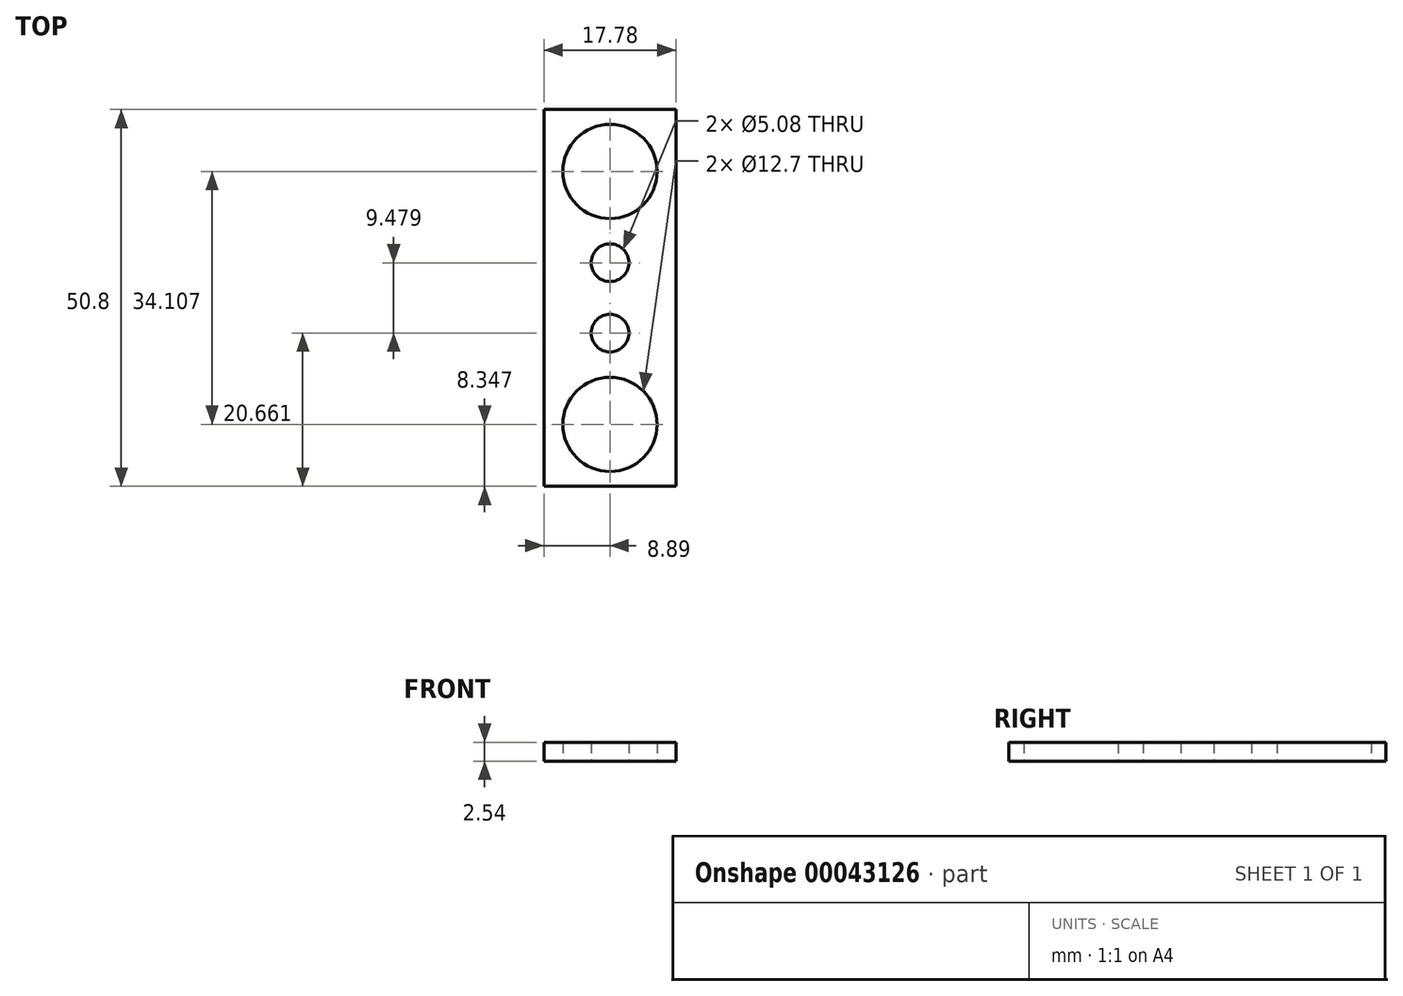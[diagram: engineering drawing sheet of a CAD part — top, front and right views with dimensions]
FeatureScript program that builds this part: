
annotation { "Feature Type Name" : "Feature", "Feature Type Description" : "" }
export const myFeature = defineFeature(function(context is Context, id is Id, definition is map)
    precondition{}
    {
        {
            var Q0;
            Q0=qCreatedBy(makeId("Top.planeOp"),FACE);
            var sketch = newSketch(context, id + "F0", { "sketchPlane" : qUnion([Q0])});
            skLineSegment(sketch, "E0.bottom", {"start": v(8.89, 25.4) * mm, "end": v(-8.9, 25.4) * mm});
            skLineSegment(sketch, "E0.top", {"start": v(8.9, -25.4) * mm, "end": v(-8.89, -25.4) * mm});
            skLineSegment(sketch, "E0.left", {"start": v(8.89, 25.4) * mm, "end": v(8.9, -25.4) * mm});
            skLineSegment(sketch, "E0.right", {"start": v(-8.9, 25.4) * mm, "end": v(-8.89, -25.4) * mm});
            skPoint(sketch, "E0.middle", {"position": v(0, 0) * mm});
            skCircle(sketch, "E1", {"center": v(0, 17.05) * mm, "radius": 6.35 * mm});
            skPoint(sketch, "E1.centerSnap0", {"position": v(0, 25.4) * mm});
            skCircle(sketch, "E2.MirrorC", {"center": v(0, -17.05) * mm, "radius": 6.35 * mm});
            skCircle(sketch, "E3", {"center": v(0, 4.74) * mm, "radius": 2.54 * mm});
            skCircle(sketch, "E4.MirrorC", {"center": v(0, -4.74) * mm, "radius": 2.54 * mm});
            skSolve(sketch);
        }
        {
            var Q0;
            Q0=makeQuery(id+"F0.imprint","IMPRINT",FACE,{"disambiguationData":[TD([[makeQuery(id+"F0.imprint","IMPRINT",EDGE,{"derivedFrom":sQuery(id+"F0.wireOp",EDGE,"E0.bottom")}),1.0]])]});
            extrude(context, id + "F1", {"entities" : qUnion([Q0]), "depth" : 2.54 * mm});
        }
    });
